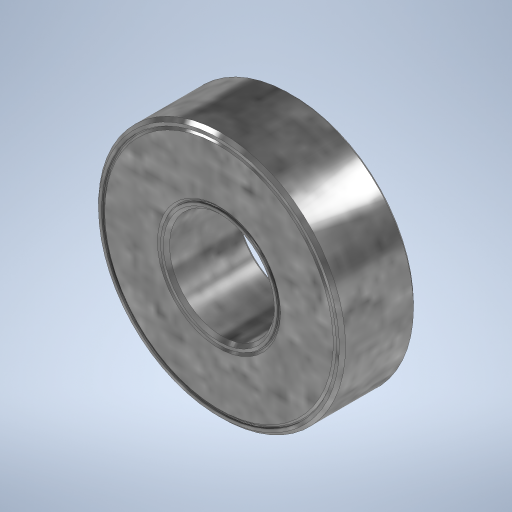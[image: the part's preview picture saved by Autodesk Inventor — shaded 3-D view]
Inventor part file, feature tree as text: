
AUTODESK INVENTOR PART (.ipt)
format: ipt  version: 2023 (Build 270158000, 158)  size: 387,072 bytes
history: native  units: mm
features: sketch x2, other x1, extrude x1, chamfer x1, revolve x1
ambient origin geometry x8: Origin, YZ Plane, XZ Plane, XY Plane, X Axis, Y Axis, Z Axis, Center Point
bodies: Body1 (feature_tree)
feature tree (6):
  other  "솔리드1"
  extrude  "돌출1"  Depth=17.0mm
  chamfer  "모따기1"  Distance=40.0mm
  revolve  "회전1"
  sketch  "스케치1"
  sketch  "스케치2"
